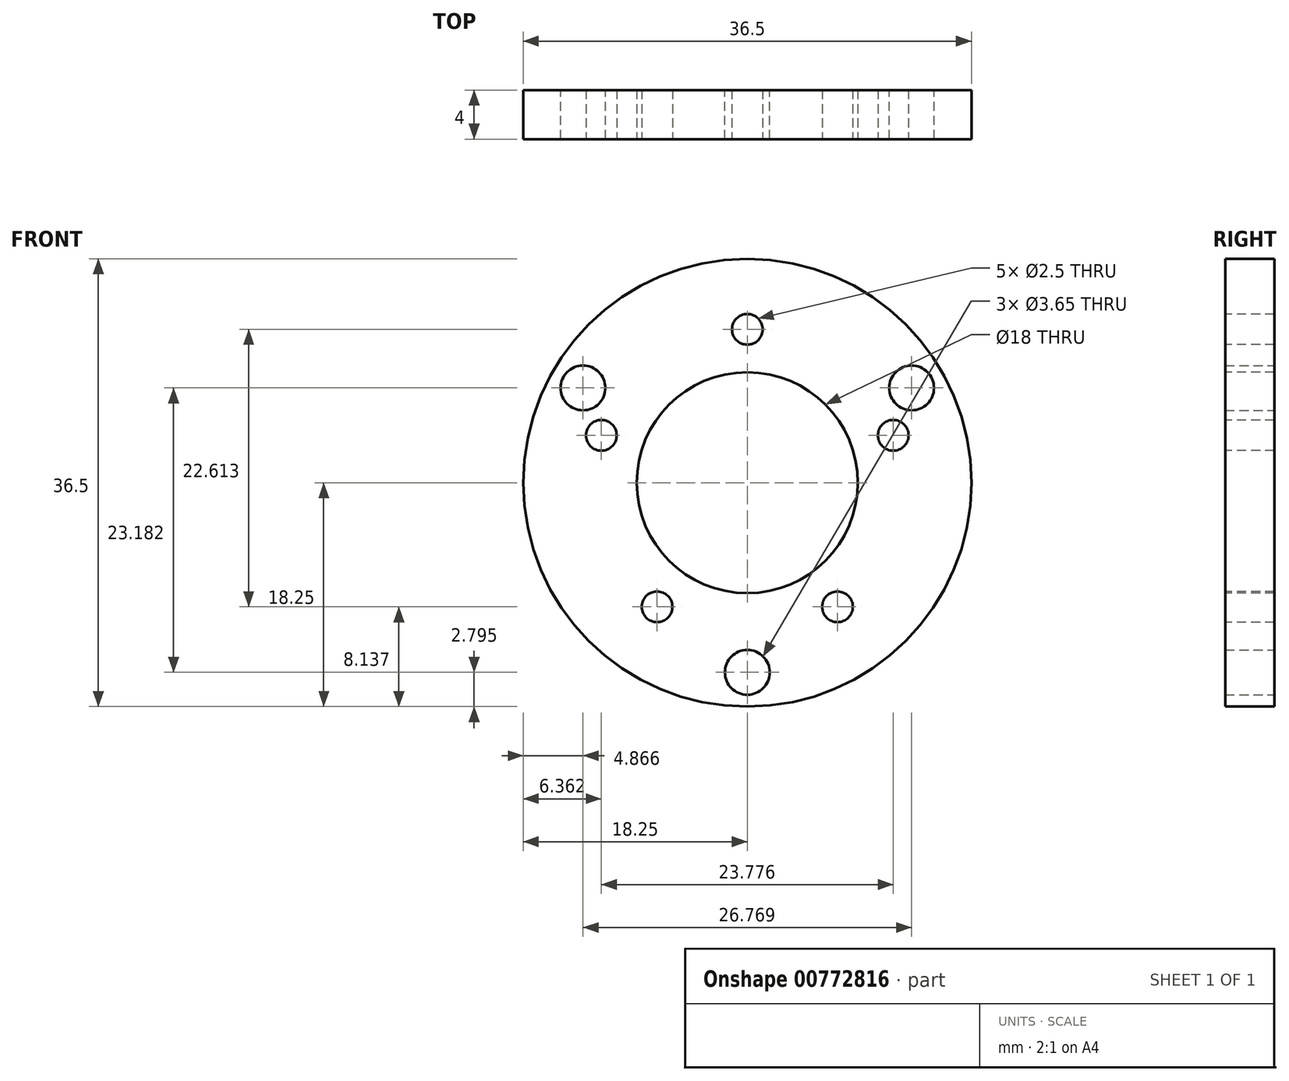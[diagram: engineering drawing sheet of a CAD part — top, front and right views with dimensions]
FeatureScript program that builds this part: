
annotation { "Feature Type Name" : "Feature", "Feature Type Description" : "" }
export const myFeature = defineFeature(function(context is Context, id is Id, definition is map)
    precondition{}
    {
        {
            var Q0;
            Q0=qCreatedBy(makeId("Front.planeOp"),FACE);
            var sketch = newSketch(context, id + "F0", { "sketchPlane" : qUnion([Q0])});
            skCircle(sketch, "E0", {"center": v(0, 0) * mm, "radius": 18.25 * mm});
            skCircle(sketch, "E1", {"center": v(0, 0) * mm, "radius": 9 * mm});
            skCircle(sketch, "E2.cCircle", {"center": v(0, 0) * mm, "radius": 12.5 * mm, "construction": true});
            skLineSegment(sketch, "E2.0", {"start": v(0, 12.5) * mm, "end": v(11.89, 3.86) * mm, "construction": true});
            skLineSegment(sketch, "E2.1", {"start": v(11.89, 3.86) * mm, "end": v(7.35, -10.11) * mm, "construction": true});
            skLineSegment(sketch, "E2.2", {"start": v(7.35, -10.11) * mm, "end": v(-7.35, -10.11) * mm, "construction": true});
            skLineSegment(sketch, "E2.3", {"start": v(-7.35, -10.11) * mm, "end": v(-11.89, 3.86) * mm, "construction": true});
            skLineSegment(sketch, "E2.4", {"start": v(-11.89, 3.86) * mm, "end": v(0, 12.5) * mm, "construction": true});
            skCircle(sketch, "E3", {"center": v(0, 12.5) * mm, "radius": 1.25 * mm});
            skCircle(sketch, "E4", {"center": v(11.89, 3.86) * mm, "radius": 1.25 * mm});
            skCircle(sketch, "E5", {"center": v(7.35, -10.11) * mm, "radius": 1.25 * mm});
            skCircle(sketch, "E6", {"center": v(-7.35, -10.11) * mm, "radius": 1.25 * mm});
            skCircle(sketch, "E7", {"center": v(-11.89, 3.86) * mm, "radius": 1.25 * mm});
            skSolve(sketch);
        }
        {
            var Q0;
            Q0=makeQuery(id+"F0.imprint","IMPRINT",FACE,{"disambiguationData":[TD([[makeQuery(id+"F0.imprint","IMPRINT",EDGE,{"derivedFrom":sQuery(id+"F0.wireOp",EDGE,"E0")}),1.0]])]});
            extrude(context, id + "F1", {"entities" : qUnion([Q0]), "oppositeDirection" : true, "depth" : 4 * mm, "offsetDistance" : 25 * mm});
        }
        {
            var Q0;
            Q0=makeQuery(id+"F1.opExtrude","CAP_FACE",FACE,{"disambiguationData":[OSD([sQuery(id+"F0.wireOp",EDGE,"E0"),sQuery(id+"F0.wireOp",EDGE,"E1"),sQuery(id+"F0.wireOp",EDGE,"E3"),sQuery(id+"F0.wireOp",EDGE,"E4"),sQuery(id+"F0.wireOp",EDGE,"E5"),sQuery(id+"F0.wireOp",EDGE,"E6"),sQuery(id+"F0.wireOp",EDGE,"E7")])],"isStart":false});
            var sketch = newSketch(context, id + "F2", { "sketchPlane" : qUnion([Q0])});
            skCircle(sketch, "E8.cCircle", {"center": v(0, 0) * mm, "radius": 15.45 * mm, "construction": true});
            skLineSegment(sketch, "E8.0", {"start": v(-13.38, -7.73) * mm, "end": v(-15.45, 0) * mm, "construction": true});
            skLineSegment(sketch, "E8.1", {"start": v(-15.45, 0) * mm, "end": v(-13.38, 7.73) * mm, "construction": true});
            skLineSegment(sketch, "E8.2", {"start": v(-13.38, 7.73) * mm, "end": v(-7.73, 13.38) * mm, "construction": true});
            skLineSegment(sketch, "E8.3", {"start": v(-7.73, 13.38) * mm, "end": v(0, 15.45) * mm, "construction": true});
            skLineSegment(sketch, "E8.4", {"start": v(0, 15.45) * mm, "end": v(7.73, 13.38) * mm, "construction": true});
            skLineSegment(sketch, "E8.5", {"start": v(7.73, 13.38) * mm, "end": v(13.38, 7.73) * mm, "construction": true});
            skLineSegment(sketch, "E8.6", {"start": v(13.38, 7.73) * mm, "end": v(15.45, 0) * mm, "construction": true});
            skLineSegment(sketch, "E8.7", {"start": v(15.45, 0) * mm, "end": v(13.38, -7.73) * mm, "construction": true});
            skLineSegment(sketch, "E8.8", {"start": v(13.38, -7.73) * mm, "end": v(7.73, -13.38) * mm, "construction": true});
            skLineSegment(sketch, "E8.9", {"start": v(7.73, -13.38) * mm, "end": v(0, -15.45) * mm, "construction": true});
            skLineSegment(sketch, "E8.10", {"start": v(0, -15.45) * mm, "end": v(-7.73, -13.38) * mm, "construction": true});
            skLineSegment(sketch, "E8.11", {"start": v(-7.73, -13.38) * mm, "end": v(-13.38, -7.73) * mm, "construction": true});
            skCircle(sketch, "E9", {"center": v(13.38, 7.73) * mm, "radius": 1.82 * mm});
            skCircle(sketch, "E10", {"center": v(-13.38, 7.73) * mm, "radius": 1.83 * mm});
            skCircle(sketch, "E11", {"center": v(0, -15.45) * mm, "radius": 1.83 * mm});
            skSolve(sketch);
        }
        {
            var Q0;
            Q0=makeQuery(id+"F2.imprint","IMPRINT",FACE,{"disambiguationData":[TD([[makeQuery(id+"F2.imprint","IMPRINT",EDGE,{"derivedFrom":sQuery(id+"F2.wireOp",EDGE,"E10")}),1.0]])]});
            var Q1;
            Q1=makeQuery(id+"F2.imprint","IMPRINT",FACE,{"disambiguationData":[TD([[makeQuery(id+"F2.imprint","IMPRINT",EDGE,{"derivedFrom":sQuery(id+"F2.wireOp",EDGE,"E9")}),1.0]])]});
            var Q2;
            Q2=makeQuery(id+"F2.imprint","IMPRINT",FACE,{"disambiguationData":[TD([[makeQuery(id+"F2.imprint","IMPRINT",EDGE,{"derivedFrom":sQuery(id+"F2.wireOp",EDGE,"E11")}),1.0]])]});
            extrude(context, id + "F3", {"entities" : qUnion([Q0, Q1, Q2]), "operationType" : NewBodyOperationType.REMOVE, "oppositeDirection" : true, "depth" : 25 * mm, "offsetDistance" : 25 * mm});
        }
    });
